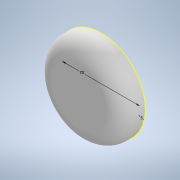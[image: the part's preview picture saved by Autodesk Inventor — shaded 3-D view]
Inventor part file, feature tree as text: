
AUTODESK INVENTOR PART (.ipt)
format: ipt  version: 2020.2 (Build 242310000, 310)  size: 125,952 bytes
history: native  units: in
note: dims shown in document units (in); Inventor stores cm internally (conversion verified against a paired STEP export)
features: sketch x2, revolve x1, fillet x1
ambient origin geometry x8: Origin, YZ Plane, XZ Plane, XY Plane, X Axis, Y Axis, Z Axis, Center Point
bodies: Solid1 (feature_tree)
feature tree (4):
  revolve  "Revolution1"  [1 undecoded]
  fillet  "Fillet1"  [1 undecoded]
  sketch  "Sketch2"  dims[d3=0.5906in d4=2.7559in d5=0.1969in]
  sketch  "Sketch1"  dims[d0=1.5748in d1=0.7874in d2=90.0deg]
note: 2 required parameter values undecoded (feature->parameter linkage not recoverable at this tier; creation-order binding heuristic only, values carry confidence <= 0.55)